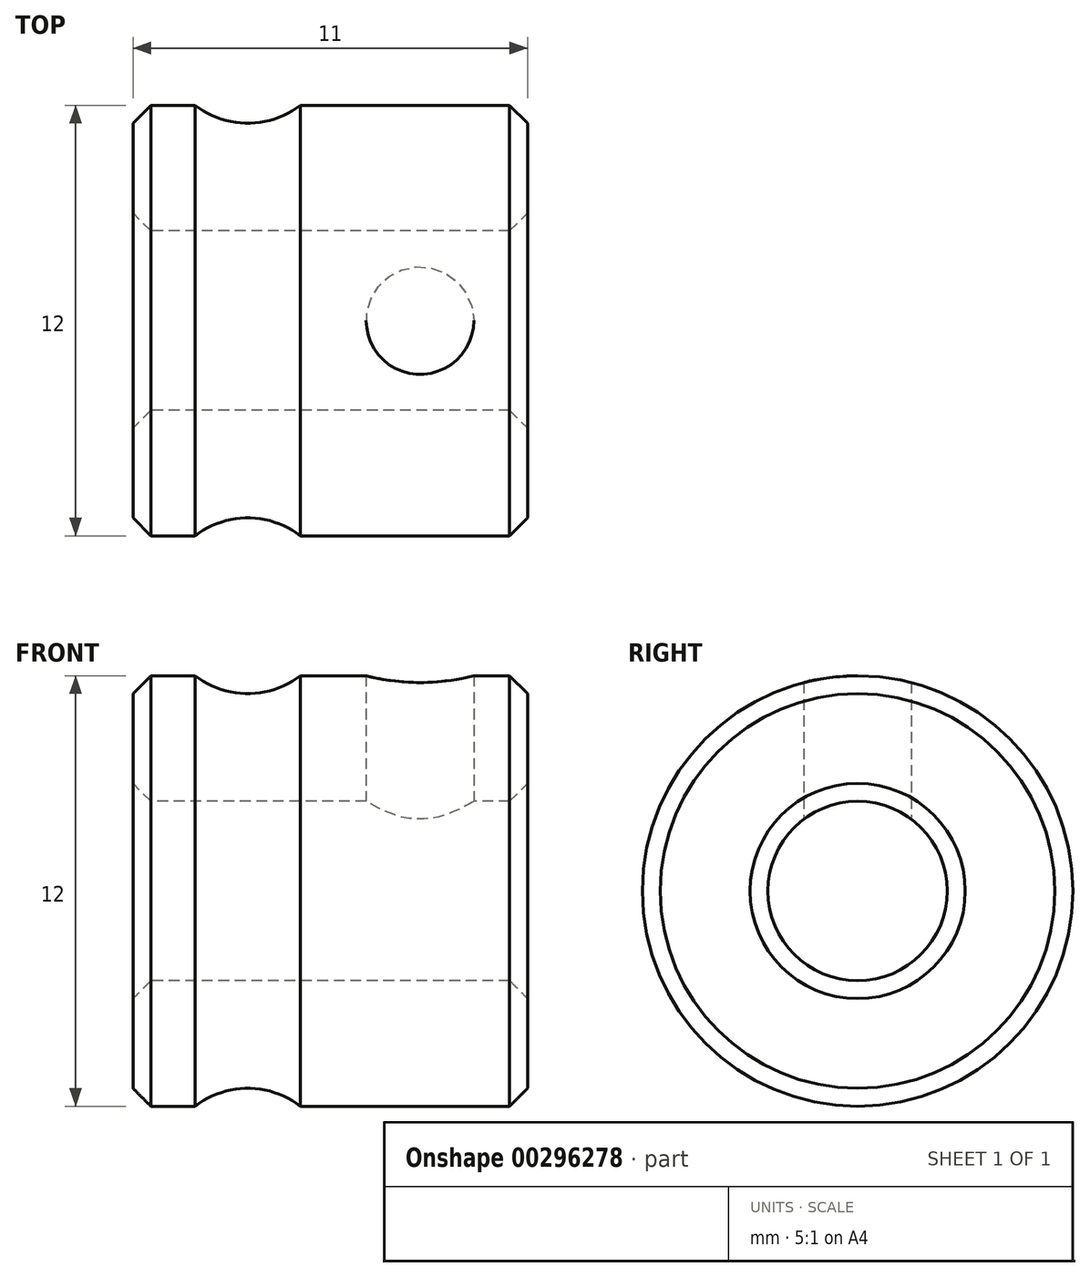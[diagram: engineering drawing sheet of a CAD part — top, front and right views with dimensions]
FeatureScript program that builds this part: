
annotation { "Feature Type Name" : "Feature", "Feature Type Description" : "" }
export const myFeature = defineFeature(function(context is Context, id is Id, definition is map)
    precondition{}
    {
        {
            var Q0;
            Q0=qCreatedBy(makeId("Top.planeOp"),FACE);
            var sketch = newSketch(context, id + "F0", { "sketchPlane" : qUnion([Q0])});
            skLineSegment(sketch, "E0.bottom", {"start": v(0, 2.5) * mm, "end": v(11, 2.5) * mm});
            skLineSegment(sketch, "E0.top", {"start": v(0, 6) * mm, "end": v(11, 6) * mm});
            skLineSegment(sketch, "E0.left", {"start": v(0, 6) * mm, "end": v(0, 2.5) * mm});
            skLineSegment(sketch, "E0.right", {"start": v(11, 6) * mm, "end": v(11, 2.5) * mm});
            skLineSegment(sketch, "E1", {"start": v(0, 0) * mm, "end": v(8, 0) * mm, "construction": true});
            skLineSegment(sketch, "E2", {"start": v(0, 0) * mm, "end": v(0, 6) * mm, "construction": true});
            skSolve(sketch);
        }
        {
            var Q0;
            Q0=makeQuery(id+"F0.imprint","IMPRINT",FACE,{"disambiguationData":[TD([[makeQuery(id+"F0.imprint","IMPRINT",EDGE,{"derivedFrom":sQuery(id+"F0.wireOp",EDGE,"E0.bottom")}),1.0]])]});
            var Q1;
            Q1=sQuery(id+"F0.wireOp",EDGE,"E1");
            revolve(context, id + "F1", {"entities" : qUnion([Q0]), "axis" : qUnion([Q1]), "revolveType" : RevolveType.FULL});
        }
        {
            var Q0;
            Q0=sQuery(id+"F0.wireOp",VERTEX,"E1.end");
            var Q1;
            Q1=makeQuery(id+"F1.opRevolve","SWEPT_BODY",BODY,{"disambiguationData":[OSD([sQuery(id+"F0.wireOp",EDGE,"E0.bottom"),sQuery(id+"F0.wireOp",EDGE,"E0.top"),sQuery(id+"F0.wireOp",EDGE,"E0.left"),sQuery(id+"F0.wireOp",EDGE,"E0.right")])]});
            hole(context, id + "F2", {"style" : HoleStyle.SIMPLE, "endStyle" : HoleEndStyle.THROUGH, "oppositeDirection" : true, "standardTappedOrClearance" : lookupTablePath({ "standard" : "ISO", "size" : "3", "type" : "Drilled" }), "standardBlindInLast" : lookupTablePath({ "standard" : "ISO", "size" : "3", "type" : "Drilled" }), "holeDiameter" : 3 * mm, "tappedDepth" : 12 * mm, "tapClearance" : 3, "locations" : qUnion([Q0]), "scope" : qUnion([Q1])});
        }
        {
            var Q0;
            Q0=qCreatedBy(makeId("Top.planeOp"),FACE);
            var sketch = newSketch(context, id + "F3", { "sketchPlane" : qUnion([Q0])});
            skCircle(sketch, "E3", {"center": v(3.2, 7.9) * mm, "radius": 2.4 * mm});
            skSolve(sketch);
        }
        {
            var Q0;
            Q0=makeQuery(id+"F3.imprint","IMPRINT",FACE,{"disambiguationData":[TD([[makeQuery(id+"F3.imprint","IMPRINT",EDGE,{"derivedFrom":sQuery(id+"F3.wireOp",EDGE,"E3")}),1.0]])]});
            var Q1;
            Q1=sQuery(id+"F0.wireOp",EDGE,"E1");
            revolve(context, id + "F4", {"operationType" : NewBodyOperationType.REMOVE, "entities" : qUnion([Q0]), "axis" : qUnion([Q1]), "revolveType" : RevolveType.FULL, "oppositeDirection" : true});
        }
        {
            var Q0;
            Q0=makeQuery(id+"F1.opRevolve","SWEPT_EDGE",EDGE,{"disambiguationData":[OSD([sQuery(id+"F0.wireOp",EDGE,"E0.top"),sQuery(id+"F0.wireOp",EDGE,"E0.left")])]});
            var Q1;
            Q1=makeQuery(id+"F1.opRevolve","SWEPT_EDGE",EDGE,{"disambiguationData":[OSD([sQuery(id+"F0.wireOp",EDGE,"E0.top"),sQuery(id+"F0.wireOp",EDGE,"E0.right")])]});
            var Q2;
            Q2=makeQuery(id+"F1.opRevolve","SWEPT_EDGE",EDGE,{"disambiguationData":[OSD([sQuery(id+"F0.wireOp",EDGE,"E0.bottom"),sQuery(id+"F0.wireOp",EDGE,"E0.left")])]});
            var Q3;
            Q3=makeQuery(id+"F1.opRevolve","SWEPT_EDGE",EDGE,{"disambiguationData":[OSD([sQuery(id+"F0.wireOp",EDGE,"E0.bottom"),sQuery(id+"F0.wireOp",EDGE,"E0.right")])]});
            var Q4;
            Q4=makeQuery(id+"F2.hole-0.boolean.opBoolean","INTERSECT",EDGE,{"derivedFrom":[makeQuery(id+"F1.opRevolve","SWEPT_FACE",FACE,{"disambiguationData":[OSD([sQuery(id+"F0.wireOp",EDGE,"E0.top")])]}),makeQuery(id+"F2.hole-0.opRevolve","SWEPT_FACE",FACE,{"disambiguationData":[OSD([sQuery(id+"F2.hole-0.sketch.wireOp",EDGE,"core_line_2")])]})]});
            chamfer(context, id + "F5", {"entities" : qUnion([Q0, Q1, Q2, Q3, Q4]), "width" : 0.5 * mm, "tangentPropagation" : true});
        }
    });
